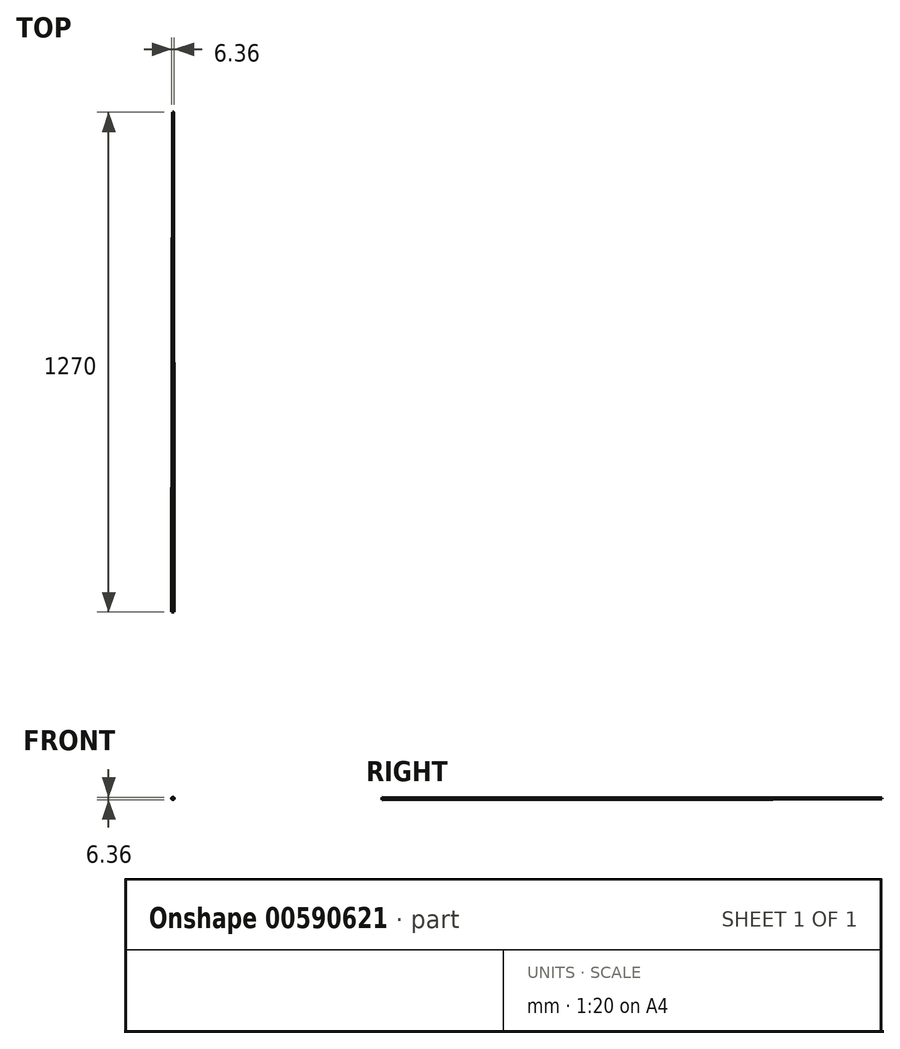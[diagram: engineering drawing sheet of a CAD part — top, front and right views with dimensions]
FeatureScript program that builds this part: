
annotation { "Feature Type Name" : "Feature", "Feature Type Description" : "" }
export const myFeature = defineFeature(function(context is Context, id is Id, definition is map)
    precondition{}
    {
        {
            var Q0;
            Q0=qCreatedBy(makeId("Front.planeOp"),FACE);
            cPlane(context, id + "F0", {"entities" : qUnion([Q0]), "cplaneType" : CPlaneType.OFFSET, "offset" : 635 * mm, "width" : 152.4 * mm, "height" : 152.4 * mm});
        }
        {
            var Q0;
            Q0=qCreatedBy(makeId("Front.planeOp"),FACE);
            cPlane(context, id + "F1", {"entities" : qUnion([Q0]), "cplaneType" : CPlaneType.OFFSET, "offset" : 635 * mm, "oppositeDirection" : true, "width" : 152.4 * mm, "height" : 152.4 * mm});
        }
        {
            var Q0;
            Q0=qCreatedBy(id+"F0.planeOp",FACE);
            var sketch = newSketch(context, id + "F2", { "sketchPlane" : qUnion([Q0])});
            skCircle(sketch, "E0", {"center": v(0, 0) * mm, "radius": 3.18 * mm});
            skSolve(sketch);
        }
        {
            var Q0;
            Q0=qCreatedBy(id+"F1.planeOp",FACE);
            var sketch = newSketch(context, id + "F3", { "sketchPlane" : qUnion([Q0])});
            skCircle(sketch, "E1", {"center": v(0, 0) * mm, "radius": 1.59 * mm});
            skSolve(sketch);
        }
        {
            var Q0;
            Q0=makeQuery(id+"F2.imprint","IMPRINT",FACE,{"disambiguationData":[TD([[makeQuery(id+"F2.imprint","IMPRINT",EDGE,{"derivedFrom":sQuery(id+"F2.wireOp",EDGE,"E0")}),1.0]])]});
            var Q1;
            Q1=makeQuery(id+"F3.imprint","IMPRINT",FACE,{"disambiguationData":[TD([[makeQuery(id+"F3.imprint","IMPRINT",EDGE,{"derivedFrom":sQuery(id+"F3.wireOp",EDGE,"E1")}),1.0]])]});
            loft(context, id + "F4", {"sheetProfilesArray" : [{ "sheetProfileEntities" : qUnion([Q0]) }, { "sheetProfileEntities" : qUnion([Q1]) }]});
        }
    });
